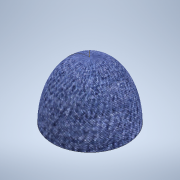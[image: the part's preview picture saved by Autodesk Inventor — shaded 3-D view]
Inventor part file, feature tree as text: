
AUTODESK INVENTOR PART (.ipt)
format: ipt  version: 2022 (Build 260153000, 153)  size: 402,432 bytes
history: native  units: in
note: dims shown in document units (in); Inventor stores cm internally (conversion verified against a paired STEP export)
features: sketch x4, other x2, revolve x1, shell x1, extrude x1, sweep x1, projected_geometry x1
ambient origin geometry x8: Origin, YZ Plane, XZ Plane, XY Plane, X Axis, Y Axis, Z Axis, Center Point
bodies: Solid1 (feature_tree)
feature tree (11):
  revolve  "Revolution1"  [1 undecoded]
  shell  "Shell1"  Thickness=90.0deg
  other  "Work Axis1"
  extrude  "Extrusion9"  Depth=0.25in
  sweep  "Sweep1"
  sketch  "Sketch1"  dims[d0=1.45in d1=2.45in d2=90.0deg]
  sketch  "Sketch13"  dims[d3=0.25in d52=1.95in]
  projected_geometry  "Projected Loop4"
  sketch  "3D Sketch1"
  other  "Helical Curve2"
  sketch  "Sketch16"  dims[d53=1.45in d54=1.7in d55=0.05in d56=0.05in d57=0.25in d58=0.0in d59=1.8in d64=0.25in d65=1.1811in d66=1.8in d67=0.0in d68=0.0in d69=0.0in d70=0.08in d40=0.5in d41=0.0344in d42=0.5in d43=0.0344in]
note: 1 required parameter value undecoded (feature->parameter linkage not recoverable at this tier; creation-order binding heuristic only, values carry confidence <= 0.55)
